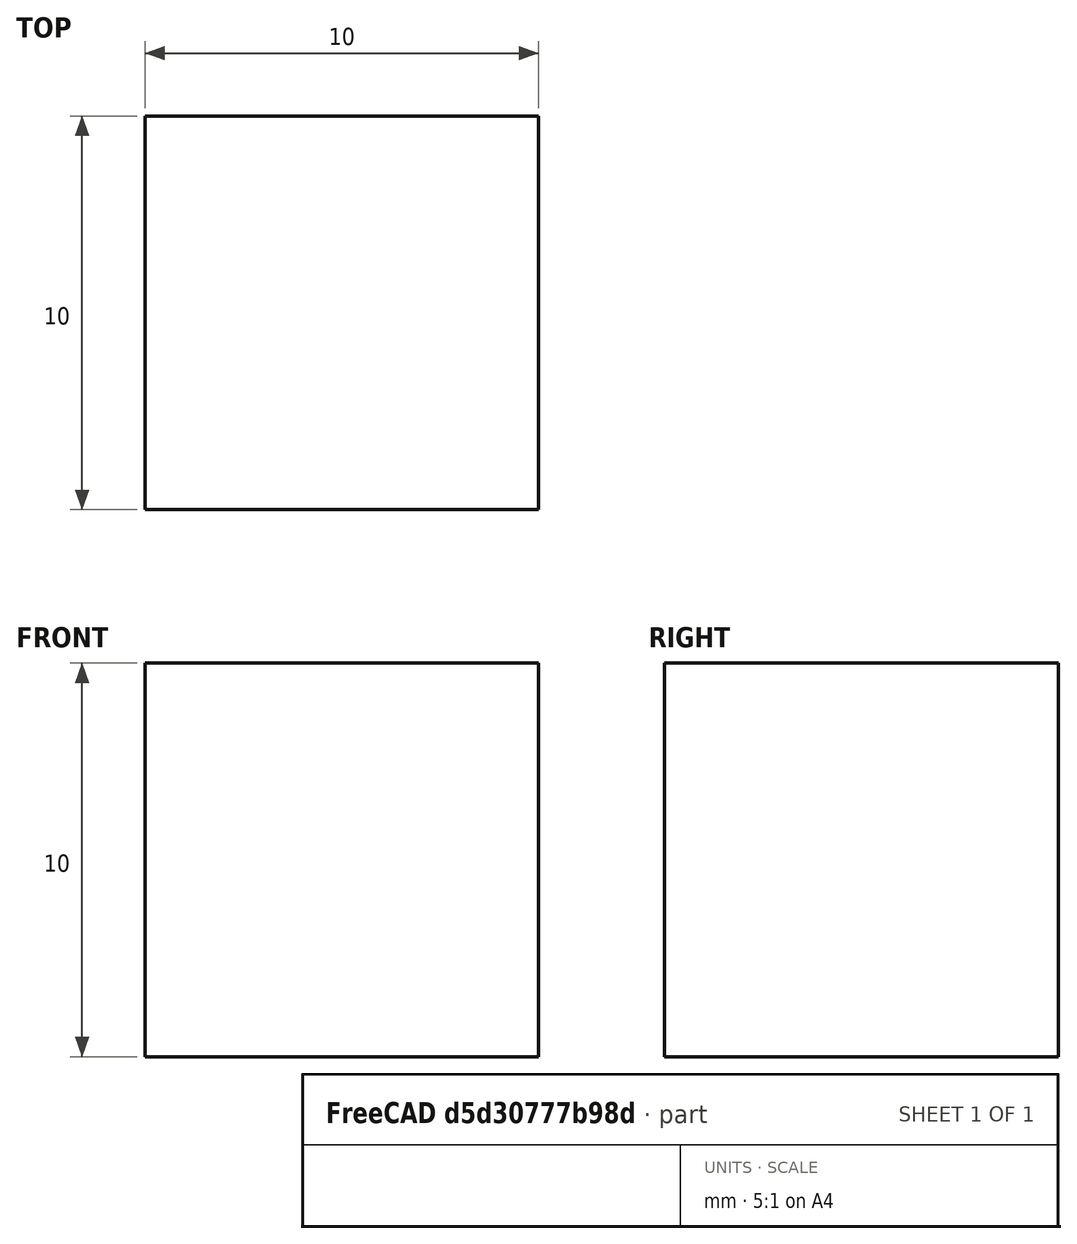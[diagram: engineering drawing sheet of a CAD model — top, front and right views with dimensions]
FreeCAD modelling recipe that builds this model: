
FCSTD DOCUMENT  (FreeCAD 0.17R10699 (Git))
Label: cube_static
License: All rights reserved
LicenseURL: http://en.wikipedia.org/wiki/All_rights_reserved
objects: Part::Box×1, Fem::FemSolverObjectPython×1, Fem::FemMeshObject×1, App::MaterialObjectPython×1, Fem::ConstraintFixed×1, Fem::ConstraintForce×1, Fem::ConstraintPressure×1, Fem::FemResultObjectPython×1, Fem::FemAnalysisPython×1
note: 1 computed .brp shape members not serialized (recipe doc carries the construction recipe); baked Part::Feature solids carry a one-line shape summary decoded from their .brp

FEATURE [Part::Box] Box
  AttacherType = Attacher::AttachEngine3D
  Height = 10
  Length = 10
  Width = 10
FEATURE [Fem::FemSolverObjectPython] CalculiX  # FEM object (typed FeaturePython)
  AnalysisType = 0
  EigenmodeHighLimit = 1000000
  EigenmodeLowLimit = 0
  EigenmodesCount = 10
  GeometricalNonlinearity = 0
  IterationsControlParameterCutb = 0.25,0.5,0.75,0.85,,,1.5,
  IterationsControlParameterIter = 4,8,9,200,10,400,,200,,
  IterationsControlParameterTimeUse = false
  IterationsThermoMechMaximum = 2000
  IterationsUserDefinedIncrementations = false
  IterationsUserDefinedTimeStepLength = 0.1, 1.0
  MaterialNonlinearity = 0
  MatrixSolverType = 0
  SolverType = FemSolverCalculix
  SplitInputWriter = false
  ThermoMechSteadyState = false
  TimeEnd = 1
  TimeInitialStep = 0.1
FEATURE [Fem::FemMeshObject] Mesh
FEATURE [App::MaterialObjectPython] MechanicalMaterial  # material (typed FeaturePython)
  Category = 0
  Material = Density=7900 kg/m^3; Name=Steel-Generic; PoissonRatio=0.30; YoungsModulus=200000 MPa
FEATURE [Fem::ConstraintFixed] FemConstraintFixed
  NormalDirection = (-1,0,0)
  Normals = (9) [(-1,0,0),(-1,0,0),(-1,0,0),(-1,0,0),(-1,0,0),(-1,0,0),(-1,0,0),(-1,0,0),(-1,0,0)]
  Points = (9) [(0,10,0),(0,10,5),(0,10,10),(0,5,0),(0,5,5),(0,5,10),(0,0,0),(0,0,5),(0,0,10)]
  References = -> [Box]
FEATURE [Fem::ConstraintForce] FemConstraintForce
  Direction = -> Box [Edge5]
  DirectionVector = (0,0,-1)
  Force = 40000
  NormalDirection = (0,0,1)
  Points = (9) [(0,0,10),(5,0,10),(10,0,10),(0,5,10),(5,5,10),(10,5,10),(0,10,10),(5,10,10),(10,10,10)]
  References = -> [Box]
  Reversed = true
FEATURE [Fem::ConstraintPressure] FemConstraintPressure
  NormalDirection = (1,0,0)
  Normals = (9) [(1,0,0),(1,0,0),(1,0,0),(1,0,0),(1,0,0),(1,0,0),(1,0,0),(1,0,0),(1,0,0)]
  Points = (9) [(10,10,0),(10,10,5),(10,10,10),(10,5,0),(10,5,5),(10,5,10),(10,0,0),(10,0,5),(10,0,10)]
  Pressure = 1000
  References = -> [Box]
FEATURE [Fem::FemResultObjectPython] CalculiX_static_results  # FEM object (typed FeaturePython)
  DisplacementLengths = [0,0,0,0,0.0935212,0.0650661,0.0937383,0.0650115,0,0,0,0,0,0,0,0,0,0,0,0,0.0745361,0.0826962,0.0689768,0.0932309,0.0933585,0.0934617,0.0745037,0.082832,0.068946,0.0630103,0.0635703,0.0635289,0.0558722,0.0337975,0.0757671,0.0327412,0.0164219,+243 more]
  DisplacementVectors = (280) [(0,0,0),(0,0,0),(0,0,0),(0,0,0),(-0.0675227,-0.00758014,-0.0642607),(-0.0242617,-0.0109484,-0.0593725),(-0.0677483,0.00776063,-0.0643181),+273 more]
  Eigenmode = 0
  EigenmodeFrequency = 0
  MaxShear = [1239.31,368.983,1240.03,353.725,509.28,515.213,508.366,516.528,611.197,845.503,501.144,1103.46,1255.33,1210.44,611.421,851.301,518.189,380.078,552.204,524.411,497.929,492.825,508.944,523.135,511.948,506.105,505.121,494.044,507.727,520.768,+250 more]
  Mesh = -> Mesh
  NodeNumbers = [1,2,3,4,5,6,7,8,9,10,11,12,13,14,15,16,17,18,19,20,21,22,23,24,25,26,27,28,29,30,31,32,33,34,35,36,37,38,39,40,41,42,43,44,45,46,47,48,49,50,51,52,53,54,55,56,57,58,59,60,61,62,63,64,65,66,67,68,69,+211 more]
  PrincipalMax = [-273.425,357.02,-279.706,344.264,49.6029,-0.634697,47.79,0.119715,-94.1008,-334.665,-6.53804,-294.547,-445.619,-412.853,-21.3047,-311.742,-54.1978,440.545,908.699,876.585,6.98646,-1.34375,-7.6521,77.5849,53.3272,38.6862,11.9885,4.34436,+252 more]
  PrincipalMed = [-1267.32,128.645,-1271.88,129.048,-20.618,-439.678,-19.705,-436.945,-731.178,-1040.77,-583.666,-1720.79,-2058.52,-1970.7,-719.24,-1067.71,-634.716,365.494,790.131,759.791,-208.69,-48.9201,-363.659,-2.79286,1.12771,2.93366,-202.195,-40.9291,+252 more]
  PrincipalMin = [-2752.04,-380.946,-2759.78,-363.186,-968.957,-1031.06,-968.943,-1032.94,-1316.49,-2025.67,-1008.83,-2501.48,-2956.29,-2833.73,-1244.15,-2014.34,-1090.58,-319.611,-195.709,-172.237,-988.872,-986.994,-1025.54,-968.686,-970.568,-973.524,+254 more]
  ResultType = FemResultMechanical
  Stats = [-0.0680669,-0.0225964,0.00296745,-0.0109484,1.47168e-05,0.0110702,-0.0643181,-0.0308767,0,0,0.039463,0.0937383,385.38,1006.74,2203.51,-445.619,75.9011,908.699,-2058.52,-363.987,790.131,-2956.29,-1040.3,-172.237,218.057,558.102,1255.33,0,0,+1 more]
  StressValues = [2160.52,654.381,2162.06,628.131,985.328,895.619,984.722,898.175,1058.94,1471.07,871.326,1938.32,2203.51,2125.13,1062.54,1477.57,899.691,725.548,1050.16,995.576,907.45,962.745,894.685,1008.49,998.819,994.816,922.001,966.246,892.453,905.608,+250 more]
  StressVectors = (280) [(-2620.33,-871.861,-800.594),(145.181,63.1739,-103.636),(-2632.4,-870.703,-808.259),(149.277,56.2241,-95.3753),(-968.956,-1.3333,30.317),+275 more]
  Time = 0
FEATURE [Fem::FemAnalysisPython] Analysis  # FEM object (typed FeaturePython)
  Member = -> [CalculiX,Mesh,MechanicalMaterial,FemConstraintFixed,FemConstraintForce,FemConstraintPressure,CalculiX_static_results]
